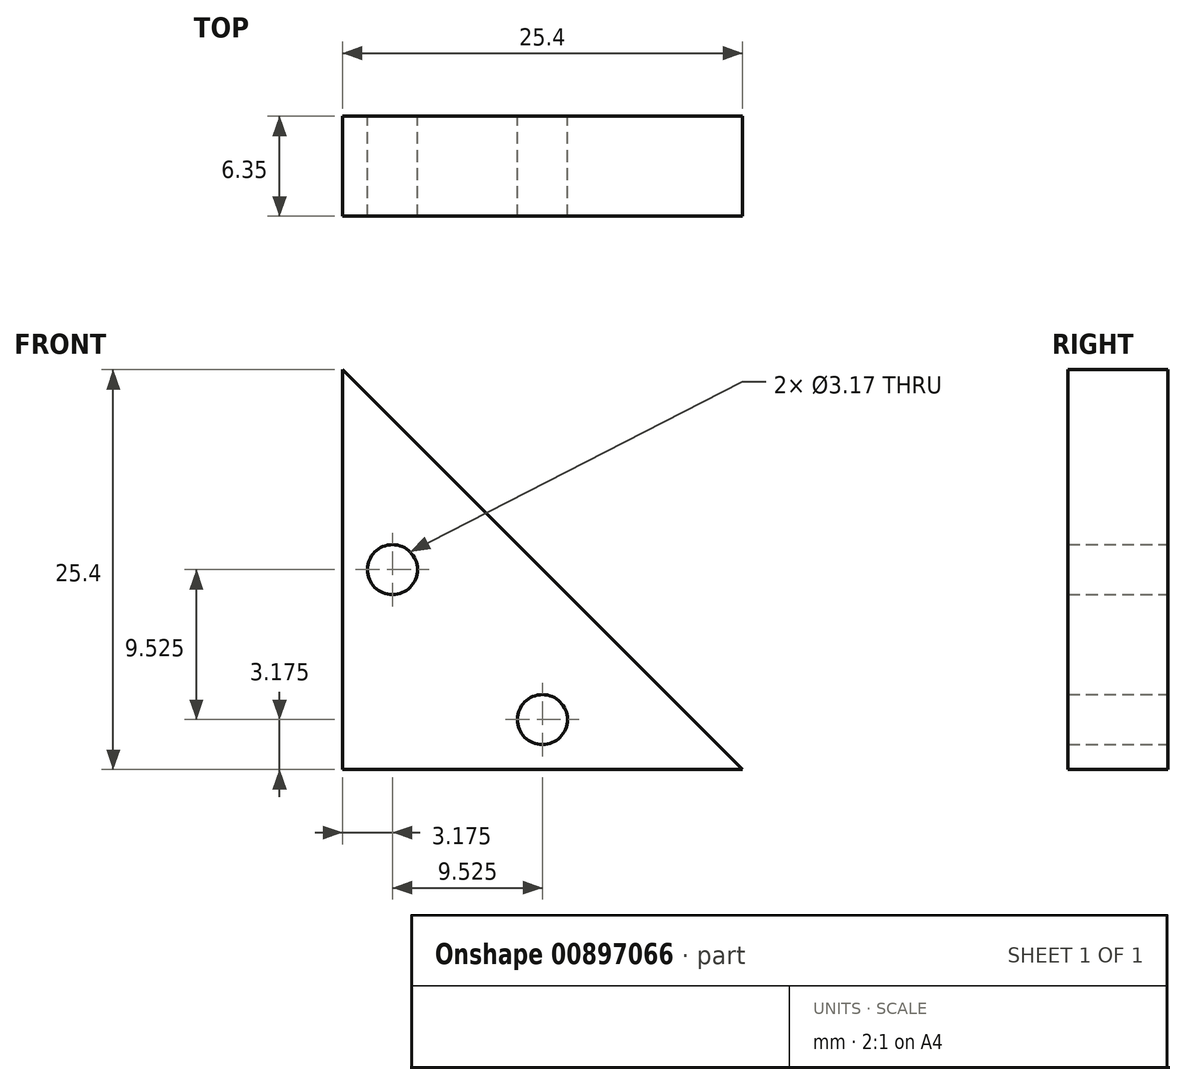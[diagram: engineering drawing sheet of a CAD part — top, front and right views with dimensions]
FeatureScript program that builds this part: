
annotation { "Feature Type Name" : "Feature", "Feature Type Description" : "" }
export const myFeature = defineFeature(function(context is Context, id is Id, definition is map)
    precondition{}
    {
        {
            var Q0;
            Q0=qCreatedBy(makeId("Front.planeOp"),FACE);
            var sketch = newSketch(context, id + "F0", { "sketchPlane" : qUnion([Q0])});
            skLineSegment(sketch, "E0", {"start": v(0, 0) * mm, "end": v(0, 25.4) * mm});
            skLineSegment(sketch, "E1", {"start": v(0, 25.4) * mm, "end": v(25.4, 0) * mm});
            skLineSegment(sketch, "E2", {"start": v(25.4, 0) * mm, "end": v(0, 0) * mm});
            skCircle(sketch, "E3", {"center": v(3.18, 12.7) * mm, "radius": 1.59 * mm});
            skCircle(sketch, "E4", {"center": v(12.7, 3.17) * mm, "radius": 1.59 * mm});
            skSolve(sketch);
        }
        {
            var Q0;
            Q0 = qSketchRegion(id + "F0", true);
            extrude(context, id + "F1", {"entities" : qUnion([Q0]), "depth" : 6.35 * mm, "offsetDistance" : 25.4 * mm});
        }
    });
